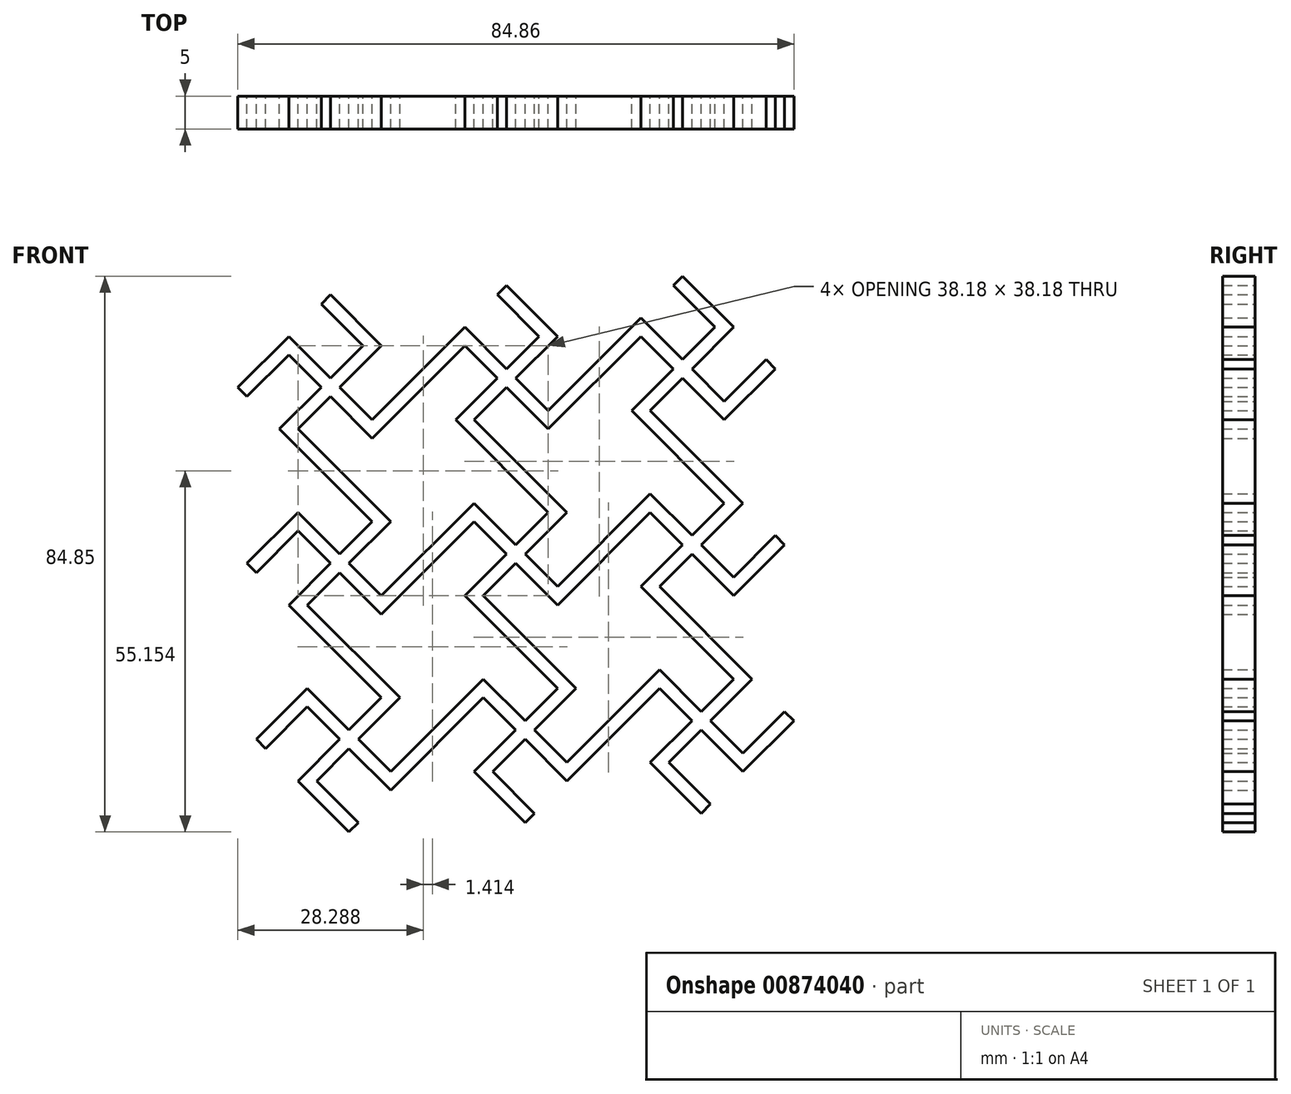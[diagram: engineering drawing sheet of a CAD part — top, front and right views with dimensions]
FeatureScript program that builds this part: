
annotation { "Feature Type Name" : "Feature", "Feature Type Description" : "" }
export const myFeature = defineFeature(function(context is Context, id is Id, definition is map)
    precondition{}
    {
        {
            var Q0;
            Q0=qCreatedBy(makeId("Front.planeOp"),FACE);
            var sketch = newSketch(context, id + "F0", { "sketchPlane" : qUnion([Q0])});
            skLineSegment(sketch, "E0", {"start": v(-7.07, 7.07) * mm, "end": v(-14.14, 0) * mm});
            skLineSegment(sketch, "E1", {"start": v(-7.07, -7.07) * mm, "end": v(0, -14.14) * mm});
            skLineSegment(sketch, "E2", {"start": v(7.07, -7.07) * mm, "end": v(14.14, 0) * mm});
            skLineSegment(sketch, "E3", {"start": v(7.07, 7.07) * mm, "end": v(0, 14.14) * mm});
            skLineSegment(sketch, "E4.bottom", {"start": v(6.36, 7.78) * mm, "end": v(7.78, 6.36) * mm});
            skLineSegment(sketch, "E4.top", {"start": v(-7.78, -6.36) * mm, "end": v(-6.36, -7.78) * mm});
            skLineSegment(sketch, "E4.left", {"start": v(4.95, 6.36) * mm, "end": v(0, 1.41) * mm});
            skLineSegment(sketch, "E4.right", {"start": v(7.78, 6.36) * mm, "end": v(1.41, 0) * mm});
            skPoint(sketch, "E4.middle", {"position": v(0, 0) * mm});
            skLineSegment(sketch, "E5.bottom", {"start": v(-6.36, 7.78) * mm, "end": v(0, 1.41) * mm});
            skLineSegment(sketch, "E5.top", {"start": v(-6.36, 4.95) * mm, "end": v(-1.41, 0) * mm});
            skLineSegment(sketch, "E5.left", {"start": v(-6.36, 7.78) * mm, "end": v(-7.78, 6.36) * mm});
            skLineSegment(sketch, "E5.right", {"start": v(7.78, -6.36) * mm, "end": v(6.36, -7.78) * mm});
            skPoint(sketch, "E6", {"position": v(-3.89, -10.25) * mm});
            skLineSegment(sketch, "E7.bottom", {"start": v(-6.36, 7.78) * mm, "end": v(-4.95, 6.36) * mm});
            skLineSegment(sketch, "E7.left", {"start": v(-6.36, 7.78) * mm, "end": v(-14.14, 0) * mm});
            skLineSegment(sketch, "E7.right", {"start": v(-6.36, 4.95) * mm, "end": v(-12.73, -1.41) * mm});
            skLineSegment(sketch, "E8.bottom", {"start": v(-7.78, -6.36) * mm, "end": v(0, -14.14) * mm});
            skLineSegment(sketch, "E8.top", {"start": v(-4.95, -6.36) * mm, "end": v(1.41, -12.73) * mm});
            skLineSegment(sketch, "E8.left", {"start": v(-7.78, -6.36) * mm, "end": v(-6.36, -4.95) * mm});
            skLineSegment(sketch, "E9.bottom", {"start": v(6.36, -7.78) * mm, "end": v(4.95, -6.36) * mm});
            skLineSegment(sketch, "E9.top", {"start": v(14.14, 0) * mm, "end": v(12.73, 1.41) * mm});
            skLineSegment(sketch, "E9.left", {"start": v(6.36, -7.78) * mm, "end": v(14.14, 0) * mm});
            skLineSegment(sketch, "E9.right", {"start": v(6.36, -4.95) * mm, "end": v(12.73, 1.41) * mm});
            skLineSegment(sketch, "E10.bottom", {"start": v(7.78, 6.36) * mm, "end": v(0, 14.14) * mm});
            skLineSegment(sketch, "E10.left", {"start": v(7.78, 6.36) * mm, "end": v(6.36, 4.95) * mm});
            skLineSegment(sketch, "E11.trimOffspring", {"start": v(4.95, 6.36) * mm, "end": v(-1.41, 12.73) * mm});
            skLineSegment(sketch, "E12.trimOffspring", {"start": v(1.41, 0) * mm, "end": v(6.36, -4.95) * mm});
            skLineSegment(sketch, "E13.trimOffspring", {"start": v(0, -1.41) * mm, "end": v(6.36, -7.78) * mm});
            skLineSegment(sketch, "E14.trimOffspring", {"start": v(0, -1.41) * mm, "end": v(-4.95, -6.36) * mm});
            skLineSegment(sketch, "E15.trimOffspring", {"start": v(-1.41, 0) * mm, "end": v(-7.78, -6.36) * mm});
            skLineSegment(sketch, "E16.0", {"start": v(12.73, 1.41) * mm, "end": v(14.14, 0) * mm, "construction": true});
            skLineSegment(sketch, "E17", {"start": v(-8.49, 33.94) * mm, "end": v(-15.56, 26.87) * mm});
            skLineSegment(sketch, "E18", {"start": v(-8.49, 19.8) * mm, "end": v(-1.41, 12.73) * mm});
            skLineSegment(sketch, "E19", {"start": v(5.66, 19.8) * mm, "end": v(12.73, 26.87) * mm});
            skLineSegment(sketch, "E20", {"start": v(5.66, 33.94) * mm, "end": v(-1.41, 41.01) * mm});
            skLineSegment(sketch, "E21.bottom", {"start": v(4.95, 34.65) * mm, "end": v(6.36, 33.23) * mm});
            skLineSegment(sketch, "E21.top", {"start": v(-9.2, 20.5) * mm, "end": v(-7.78, 19.1) * mm});
            skLineSegment(sketch, "E21.left", {"start": v(3.54, 33.23) * mm, "end": v(-1.41, 28.28) * mm});
            skLineSegment(sketch, "E21.right", {"start": v(6.36, 33.23) * mm, "end": v(0, 26.87) * mm});
            skPoint(sketch, "E21.middle", {"position": v(-1.41, 26.87) * mm});
            skLineSegment(sketch, "E22.bottom", {"start": v(-7.78, 34.65) * mm, "end": v(-1.41, 28.28) * mm});
            skLineSegment(sketch, "E22.top", {"start": v(-7.78, 31.82) * mm, "end": v(-2.83, 26.87) * mm});
            skLineSegment(sketch, "E22.left", {"start": v(-7.78, 34.65) * mm, "end": v(-9.2, 33.23) * mm});
            skLineSegment(sketch, "E22.right", {"start": v(6.36, 20.5) * mm, "end": v(4.95, 19.1) * mm});
            skPoint(sketch, "E23", {"position": v(-5.3, 16.62) * mm});
            skLineSegment(sketch, "E24.bottom", {"start": v(-7.78, 34.65) * mm, "end": v(-6.36, 33.23) * mm});
            skLineSegment(sketch, "E24.left", {"start": v(-7.78, 34.65) * mm, "end": v(-15.56, 26.87) * mm});
            skLineSegment(sketch, "E24.right", {"start": v(-7.78, 31.82) * mm, "end": v(-14.14, 25.46) * mm});
            skLineSegment(sketch, "E25.bottom", {"start": v(-9.2, 20.5) * mm, "end": v(-1.41, 12.73) * mm});
            skLineSegment(sketch, "E25.top", {"start": v(-6.36, 20.5) * mm, "end": v(0, 14.14) * mm});
            skLineSegment(sketch, "E25.left", {"start": v(-9.2, 20.5) * mm, "end": v(-7.78, 21.92) * mm});
            skLineSegment(sketch, "E26.bottom", {"start": v(4.95, 19.1) * mm, "end": v(3.54, 20.5) * mm});
            skLineSegment(sketch, "E26.top", {"start": v(12.73, 26.87) * mm, "end": v(11.31, 28.28) * mm});
            skLineSegment(sketch, "E26.left", {"start": v(4.95, 19.1) * mm, "end": v(12.73, 26.87) * mm});
            skLineSegment(sketch, "E26.right", {"start": v(4.95, 21.92) * mm, "end": v(11.31, 28.28) * mm});
            skLineSegment(sketch, "E27.bottom", {"start": v(6.36, 33.23) * mm, "end": v(-1.41, 41.01) * mm});
            skLineSegment(sketch, "E27.left", {"start": v(6.36, 33.23) * mm, "end": v(4.95, 31.82) * mm});
            skLineSegment(sketch, "E27.right", {"start": v(-1.41, 41.01) * mm, "end": v(-2.83, 39.6) * mm});
            skLineSegment(sketch, "E28.trimOffspring", {"start": v(3.54, 33.23) * mm, "end": v(-2.83, 39.6) * mm});
            skLineSegment(sketch, "E29.trimOffspring", {"start": v(0, 26.87) * mm, "end": v(4.95, 21.92) * mm});
            skLineSegment(sketch, "E30.trimOffspring", {"start": v(-1.41, 25.46) * mm, "end": v(4.95, 19.1) * mm});
            skLineSegment(sketch, "E31.trimOffspring", {"start": v(-1.41, 25.46) * mm, "end": v(-6.36, 20.5) * mm});
            skLineSegment(sketch, "E32.trimOffspring", {"start": v(-2.83, 26.87) * mm, "end": v(-9.2, 20.5) * mm});
            skLineSegment(sketch, "E33.0", {"start": v(11.31, 28.28) * mm, "end": v(12.73, 26.87) * mm, "construction": true});
            skLineSegment(sketch, "E34", {"start": v(-33.94, -8.49) * mm, "end": v(-26.87, -15.56) * mm});
            skLineSegment(sketch, "E35", {"start": v(-19.8, -8.49) * mm, "end": v(-12.73, -1.41) * mm});
            skLineSegment(sketch, "E36", {"start": v(-19.8, 5.66) * mm, "end": v(-26.87, 12.73) * mm});
            skLineSegment(sketch, "E37.bottom", {"start": v(-20.5, 6.36) * mm, "end": v(-19.1, 4.95) * mm});
            skLineSegment(sketch, "E37.top", {"start": v(-34.65, -7.78) * mm, "end": v(-33.23, -9.2) * mm});
            skLineSegment(sketch, "E37.left", {"start": v(-21.92, 4.95) * mm, "end": v(-26.87, 0) * mm});
            skLineSegment(sketch, "E37.right", {"start": v(-19.1, 4.95) * mm, "end": v(-25.46, -1.41) * mm});
            skPoint(sketch, "E37.middle", {"position": v(-26.87, -1.41) * mm});
            skLineSegment(sketch, "E38.bottom", {"start": v(-33.23, 6.36) * mm, "end": v(-26.87, 0) * mm});
            skLineSegment(sketch, "E38.top", {"start": v(-33.23, 3.54) * mm, "end": v(-28.28, -1.41) * mm});
            skLineSegment(sketch, "E38.left", {"start": v(-33.23, 6.36) * mm, "end": v(-34.65, 4.95) * mm});
            skLineSegment(sketch, "E38.right", {"start": v(-19.1, -7.78) * mm, "end": v(-20.5, -9.2) * mm});
            skPoint(sketch, "E39", {"position": v(-30.76, -11.67) * mm});
            skLineSegment(sketch, "E40.bottom", {"start": v(-33.23, 6.36) * mm, "end": v(-31.82, 4.95) * mm});
            skLineSegment(sketch, "E40.left", {"start": v(-33.23, 6.36) * mm, "end": v(-41.01, -1.41) * mm});
            skLineSegment(sketch, "E40.right", {"start": v(-33.23, 3.54) * mm, "end": v(-39.6, -2.83) * mm});
            skLineSegment(sketch, "E41.bottom", {"start": v(-34.65, -7.78) * mm, "end": v(-26.87, -15.56) * mm});
            skLineSegment(sketch, "E41.top", {"start": v(-31.82, -7.78) * mm, "end": v(-25.46, -14.14) * mm});
            skLineSegment(sketch, "E41.left", {"start": v(-34.65, -7.78) * mm, "end": v(-33.23, -6.36) * mm});
            skLineSegment(sketch, "E42.left", {"start": v(-20.5, -9.2) * mm, "end": v(-12.73, -1.41) * mm});
            skLineSegment(sketch, "E42.right", {"start": v(-20.5, -6.36) * mm, "end": v(-14.14, 0) * mm});
            skLineSegment(sketch, "E43.bottom", {"start": v(-19.1, 4.95) * mm, "end": v(-26.87, 12.73) * mm});
            skLineSegment(sketch, "E43.left", {"start": v(-19.1, 4.95) * mm, "end": v(-20.5, 3.54) * mm});
            skLineSegment(sketch, "E44.trimOffspring", {"start": v(-21.92, 4.95) * mm, "end": v(-28.28, 11.31) * mm});
            skLineSegment(sketch, "E45.trimOffspring", {"start": v(-25.46, -1.41) * mm, "end": v(-20.5, -6.36) * mm});
            skLineSegment(sketch, "E46.trimOffspring", {"start": v(-26.87, -2.83) * mm, "end": v(-20.5, -9.2) * mm});
            skLineSegment(sketch, "E47.trimOffspring", {"start": v(-26.87, -2.83) * mm, "end": v(-31.82, -7.78) * mm});
            skLineSegment(sketch, "E48.trimOffspring", {"start": v(-28.28, -1.41) * mm, "end": v(-34.65, -7.78) * mm});
            skLineSegment(sketch, "E49", {"start": v(-35.36, 32.53) * mm, "end": v(-42.43, 25.46) * mm});
            skLineSegment(sketch, "E50", {"start": v(-35.36, 18.38) * mm, "end": v(-28.28, 11.31) * mm});
            skLineSegment(sketch, "E51", {"start": v(-21.21, 18.38) * mm, "end": v(-14.14, 25.46) * mm});
            skLineSegment(sketch, "E52", {"start": v(-21.21, 32.53) * mm, "end": v(-28.28, 39.6) * mm});
            skLineSegment(sketch, "E53.bottom", {"start": v(-21.92, 33.23) * mm, "end": v(-20.5, 31.82) * mm});
            skLineSegment(sketch, "E53.top", {"start": v(-36.06, 19.1) * mm, "end": v(-34.65, 17.68) * mm});
            skLineSegment(sketch, "E53.left", {"start": v(-23.33, 31.82) * mm, "end": v(-28.28, 26.87) * mm});
            skLineSegment(sketch, "E53.right", {"start": v(-20.5, 31.82) * mm, "end": v(-26.87, 25.46) * mm});
            skPoint(sketch, "E53.middle", {"position": v(-28.28, 25.46) * mm});
            skLineSegment(sketch, "E54.bottom", {"start": v(-34.65, 33.23) * mm, "end": v(-28.28, 26.87) * mm});
            skLineSegment(sketch, "E54.top", {"start": v(-34.65, 30.4) * mm, "end": v(-29.7, 25.46) * mm});
            skLineSegment(sketch, "E54.left", {"start": v(-34.65, 33.23) * mm, "end": v(-36.06, 31.82) * mm});
            skLineSegment(sketch, "E54.right", {"start": v(-20.5, 19.1) * mm, "end": v(-21.92, 17.68) * mm});
            skPoint(sketch, "E55", {"position": v(-32.17, 15.2) * mm});
            skLineSegment(sketch, "E56.bottom", {"start": v(-34.65, 33.23) * mm, "end": v(-33.23, 31.82) * mm});
            skLineSegment(sketch, "E56.left", {"start": v(-34.65, 33.23) * mm, "end": v(-42.43, 25.46) * mm});
            skLineSegment(sketch, "E56.right", {"start": v(-34.65, 30.4) * mm, "end": v(-41.01, 24.04) * mm});
            skLineSegment(sketch, "E57.bottom", {"start": v(-36.06, 19.1) * mm, "end": v(-28.28, 11.31) * mm});
            skLineSegment(sketch, "E57.top", {"start": v(-33.23, 19.1) * mm, "end": v(-26.87, 12.73) * mm});
            skLineSegment(sketch, "E57.left", {"start": v(-36.06, 19.1) * mm, "end": v(-34.65, 20.5) * mm});
            skLineSegment(sketch, "E58.bottom", {"start": v(-21.92, 17.68) * mm, "end": v(-23.33, 19.1) * mm});
            skLineSegment(sketch, "E58.left", {"start": v(-21.92, 17.68) * mm, "end": v(-14.14, 25.46) * mm});
            skLineSegment(sketch, "E58.right", {"start": v(-21.92, 20.5) * mm, "end": v(-15.56, 26.87) * mm});
            skLineSegment(sketch, "E59.bottom", {"start": v(-20.5, 31.82) * mm, "end": v(-28.28, 39.6) * mm});
            skLineSegment(sketch, "E59.left", {"start": v(-20.5, 31.82) * mm, "end": v(-21.92, 30.4) * mm});
            skLineSegment(sketch, "E59.right", {"start": v(-28.28, 39.6) * mm, "end": v(-29.7, 38.18) * mm});
            skLineSegment(sketch, "E60.trimOffspring", {"start": v(-23.33, 31.82) * mm, "end": v(-29.7, 38.18) * mm});
            skLineSegment(sketch, "E61.trimOffspring", {"start": v(-26.87, 25.46) * mm, "end": v(-21.92, 20.5) * mm});
            skLineSegment(sketch, "E62.trimOffspring", {"start": v(-28.28, 24.04) * mm, "end": v(-21.92, 17.68) * mm});
            skLineSegment(sketch, "E63.trimOffspring", {"start": v(-28.28, 24.04) * mm, "end": v(-33.23, 19.1) * mm});
            skLineSegment(sketch, "E64.trimOffspring", {"start": v(-29.7, 25.46) * mm, "end": v(-36.06, 19.1) * mm});
            skLineSegment(sketch, "E65", {"start": v(-62.23, 31.11) * mm, "end": v(-69.3, 24.04) * mm});
            skLineSegment(sketch, "E66", {"start": v(-62.23, 16.97) * mm, "end": v(-55.15, 9.9) * mm});
            skLineSegment(sketch, "E67", {"start": v(-48.08, 16.97) * mm, "end": v(-41.01, 24.04) * mm});
            skLineSegment(sketch, "E68", {"start": v(-48.08, 31.11) * mm, "end": v(-55.15, 38.18) * mm});
            skLineSegment(sketch, "E69.bottom", {"start": v(-48.8, 31.82) * mm, "end": v(-47.38, 30.4) * mm});
            skLineSegment(sketch, "E69.top", {"start": v(-62.93, 17.68) * mm, "end": v(-61.52, 16.26) * mm});
            skLineSegment(sketch, "E69.left", {"start": v(-50.2, 30.4) * mm, "end": v(-55.15, 25.46) * mm});
            skLineSegment(sketch, "E69.right", {"start": v(-47.38, 30.4) * mm, "end": v(-53.74, 24.04) * mm});
            skPoint(sketch, "E69.middle", {"position": v(-55.15, 24.04) * mm});
            skLineSegment(sketch, "E70.bottom", {"start": v(-61.52, 31.82) * mm, "end": v(-55.15, 25.46) * mm});
            skLineSegment(sketch, "E70.top", {"start": v(-61.52, 29) * mm, "end": v(-56.57, 24.04) * mm});
            skLineSegment(sketch, "E70.left", {"start": v(-61.52, 31.82) * mm, "end": v(-62.93, 30.4) * mm});
            skLineSegment(sketch, "E70.right", {"start": v(-47.38, 17.68) * mm, "end": v(-48.8, 16.26) * mm});
            skPoint(sketch, "E71", {"position": v(-59.04, 13.79) * mm});
            skLineSegment(sketch, "E72.bottom", {"start": v(-61.52, 31.82) * mm, "end": v(-60.1, 30.4) * mm});
            skLineSegment(sketch, "E72.top", {"start": v(-69.3, 24.04) * mm, "end": v(-67.88, 22.63) * mm});
            skLineSegment(sketch, "E72.left", {"start": v(-61.52, 31.82) * mm, "end": v(-69.3, 24.04) * mm});
            skLineSegment(sketch, "E72.right", {"start": v(-61.52, 29) * mm, "end": v(-67.88, 22.63) * mm});
            skLineSegment(sketch, "E73.bottom", {"start": v(-62.93, 17.68) * mm, "end": v(-55.15, 9.9) * mm});
            skLineSegment(sketch, "E73.top", {"start": v(-60.1, 17.68) * mm, "end": v(-53.74, 11.31) * mm});
            skLineSegment(sketch, "E73.left", {"start": v(-62.93, 17.68) * mm, "end": v(-61.52, 19.1) * mm});
            skLineSegment(sketch, "E74.bottom", {"start": v(-48.8, 16.26) * mm, "end": v(-50.2, 17.68) * mm});
            skLineSegment(sketch, "E74.left", {"start": v(-48.8, 16.26) * mm, "end": v(-41.01, 24.04) * mm});
            skLineSegment(sketch, "E74.right", {"start": v(-48.8, 19.1) * mm, "end": v(-42.43, 25.46) * mm});
            skLineSegment(sketch, "E75.bottom", {"start": v(-47.38, 30.4) * mm, "end": v(-55.15, 38.18) * mm});
            skLineSegment(sketch, "E75.left", {"start": v(-47.38, 30.4) * mm, "end": v(-48.8, 29) * mm});
            skLineSegment(sketch, "E75.right", {"start": v(-55.15, 38.18) * mm, "end": v(-56.57, 36.77) * mm});
            skLineSegment(sketch, "E76.trimOffspring", {"start": v(-50.2, 30.4) * mm, "end": v(-56.57, 36.77) * mm});
            skLineSegment(sketch, "E77.trimOffspring", {"start": v(-53.74, 24.04) * mm, "end": v(-48.8, 19.1) * mm});
            skLineSegment(sketch, "E78.trimOffspring", {"start": v(-55.15, 22.63) * mm, "end": v(-48.8, 16.26) * mm});
            skLineSegment(sketch, "E79.trimOffspring", {"start": v(-55.15, 22.63) * mm, "end": v(-60.1, 17.68) * mm});
            skLineSegment(sketch, "E80.trimOffspring", {"start": v(-56.57, 24.04) * mm, "end": v(-62.93, 17.68) * mm});
            skLineSegment(sketch, "E81.0", {"start": v(-69.3, 24.04) * mm, "end": v(-67.88, 22.63) * mm, "construction": true});
            skLineSegment(sketch, "E82", {"start": v(-60.81, 4.24) * mm, "end": v(-67.88, -2.83) * mm});
            skLineSegment(sketch, "E83", {"start": v(-60.81, -9.9) * mm, "end": v(-53.74, -16.97) * mm});
            skLineSegment(sketch, "E84", {"start": v(-46.67, -9.9) * mm, "end": v(-39.6, -2.83) * mm});
            skLineSegment(sketch, "E85", {"start": v(-46.67, 4.24) * mm, "end": v(-53.74, 11.31) * mm});
            skLineSegment(sketch, "E86.bottom", {"start": v(-47.38, 4.95) * mm, "end": v(-45.96, 3.54) * mm});
            skLineSegment(sketch, "E86.top", {"start": v(-61.52, -9.2) * mm, "end": v(-60.1, -10.6) * mm});
            skLineSegment(sketch, "E86.left", {"start": v(-48.8, 3.54) * mm, "end": v(-53.74, -1.41) * mm});
            skLineSegment(sketch, "E86.right", {"start": v(-45.96, 3.54) * mm, "end": v(-52.33, -2.83) * mm});
            skPoint(sketch, "E86.middle", {"position": v(-53.74, -2.83) * mm});
            skLineSegment(sketch, "E87.bottom", {"start": v(-60.1, 4.95) * mm, "end": v(-53.74, -1.41) * mm});
            skLineSegment(sketch, "E87.top", {"start": v(-60.1, 2.12) * mm, "end": v(-55.15, -2.83) * mm});
            skLineSegment(sketch, "E87.left", {"start": v(-60.1, 4.95) * mm, "end": v(-61.52, 3.54) * mm});
            skLineSegment(sketch, "E87.right", {"start": v(-45.96, -9.2) * mm, "end": v(-47.38, -10.6) * mm});
            skPoint(sketch, "E88", {"position": v(-57.63, -13.08) * mm});
            skLineSegment(sketch, "E89.bottom", {"start": v(-60.1, 4.95) * mm, "end": v(-58.69, 3.54) * mm});
            skLineSegment(sketch, "E89.top", {"start": v(-67.88, -2.83) * mm, "end": v(-66.47, -4.24) * mm});
            skLineSegment(sketch, "E89.left", {"start": v(-60.1, 4.95) * mm, "end": v(-67.88, -2.83) * mm});
            skLineSegment(sketch, "E89.right", {"start": v(-60.1, 2.12) * mm, "end": v(-66.47, -4.24) * mm});
            skLineSegment(sketch, "E90.bottom", {"start": v(-61.52, -9.2) * mm, "end": v(-53.74, -16.97) * mm});
            skLineSegment(sketch, "E90.top", {"start": v(-58.69, -9.2) * mm, "end": v(-52.33, -15.56) * mm});
            skLineSegment(sketch, "E90.left", {"start": v(-61.52, -9.2) * mm, "end": v(-60.1, -7.78) * mm});
            skLineSegment(sketch, "E91.bottom", {"start": v(-47.38, -10.6) * mm, "end": v(-48.8, -9.2) * mm});
            skLineSegment(sketch, "E91.left", {"start": v(-47.38, -10.6) * mm, "end": v(-39.6, -2.83) * mm});
            skLineSegment(sketch, "E91.right", {"start": v(-47.38, -7.78) * mm, "end": v(-41.01, -1.41) * mm});
            skLineSegment(sketch, "E92.bottom", {"start": v(-45.96, 3.54) * mm, "end": v(-53.74, 11.31) * mm});
            skLineSegment(sketch, "E92.left", {"start": v(-45.96, 3.54) * mm, "end": v(-47.38, 2.12) * mm});
            skLineSegment(sketch, "E93.trimOffspring", {"start": v(-48.8, 3.54) * mm, "end": v(-55.15, 9.9) * mm});
            skLineSegment(sketch, "E94.trimOffspring", {"start": v(-52.33, -2.83) * mm, "end": v(-47.38, -7.78) * mm});
            skLineSegment(sketch, "E95.trimOffspring", {"start": v(-53.74, -4.24) * mm, "end": v(-47.38, -10.6) * mm});
            skLineSegment(sketch, "E96.trimOffspring", {"start": v(-53.74, -4.24) * mm, "end": v(-58.69, -9.2) * mm});
            skLineSegment(sketch, "E97.trimOffspring", {"start": v(-55.15, -2.83) * mm, "end": v(-61.52, -9.2) * mm});
            skLineSegment(sketch, "E98", {"start": v(-59.4, -22.63) * mm, "end": v(-66.47, -29.7) * mm});
            skLineSegment(sketch, "E99", {"start": v(-59.4, -36.77) * mm, "end": v(-52.33, -43.84) * mm});
            skLineSegment(sketch, "E100", {"start": v(-45.25, -36.77) * mm, "end": v(-38.18, -29.7) * mm});
            skLineSegment(sketch, "E101", {"start": v(-45.25, -22.63) * mm, "end": v(-52.33, -15.56) * mm});
            skLineSegment(sketch, "E102.bottom", {"start": v(-45.96, -21.92) * mm, "end": v(-44.55, -23.33) * mm});
            skLineSegment(sketch, "E102.top", {"start": v(-60.1, -36.06) * mm, "end": v(-58.69, -37.48) * mm});
            skLineSegment(sketch, "E102.left", {"start": v(-47.38, -23.33) * mm, "end": v(-52.33, -28.28) * mm});
            skLineSegment(sketch, "E102.right", {"start": v(-44.55, -23.33) * mm, "end": v(-50.91, -29.7) * mm});
            skPoint(sketch, "E102.middle", {"position": v(-52.33, -29.7) * mm});
            skLineSegment(sketch, "E103.bottom", {"start": v(-58.69, -21.92) * mm, "end": v(-52.33, -28.28) * mm});
            skLineSegment(sketch, "E103.top", {"start": v(-58.69, -24.75) * mm, "end": v(-53.74, -29.7) * mm});
            skLineSegment(sketch, "E103.left", {"start": v(-58.69, -21.92) * mm, "end": v(-60.1, -23.33) * mm});
            skLineSegment(sketch, "E103.right", {"start": v(-44.55, -36.06) * mm, "end": v(-45.96, -37.48) * mm});
            skPoint(sketch, "E104", {"position": v(-56.21, -39.95) * mm});
            skLineSegment(sketch, "E105.bottom", {"start": v(-58.69, -21.92) * mm, "end": v(-57.28, -23.33) * mm});
            skLineSegment(sketch, "E105.top", {"start": v(-66.47, -29.7) * mm, "end": v(-65.05, -31.11) * mm});
            skLineSegment(sketch, "E105.left", {"start": v(-58.69, -21.92) * mm, "end": v(-66.47, -29.7) * mm});
            skLineSegment(sketch, "E105.right", {"start": v(-58.69, -24.75) * mm, "end": v(-65.05, -31.11) * mm});
            skLineSegment(sketch, "E106.bottom", {"start": v(-60.1, -36.06) * mm, "end": v(-52.33, -43.84) * mm});
            skLineSegment(sketch, "E106.top", {"start": v(-57.28, -36.06) * mm, "end": v(-50.91, -42.43) * mm});
            skLineSegment(sketch, "E106.left", {"start": v(-60.1, -36.06) * mm, "end": v(-58.69, -34.65) * mm});
            skLineSegment(sketch, "E106.right", {"start": v(-52.33, -43.84) * mm, "end": v(-50.91, -42.43) * mm});
            skLineSegment(sketch, "E107.bottom", {"start": v(-45.96, -37.48) * mm, "end": v(-47.38, -36.06) * mm});
            skLineSegment(sketch, "E107.left", {"start": v(-45.96, -37.48) * mm, "end": v(-38.18, -29.7) * mm});
            skLineSegment(sketch, "E107.right", {"start": v(-45.96, -34.65) * mm, "end": v(-39.6, -28.28) * mm});
            skLineSegment(sketch, "E108.bottom", {"start": v(-44.55, -23.33) * mm, "end": v(-52.33, -15.56) * mm});
            skLineSegment(sketch, "E108.left", {"start": v(-44.55, -23.33) * mm, "end": v(-45.96, -24.75) * mm});
            skLineSegment(sketch, "E109.trimOffspring", {"start": v(-47.38, -23.33) * mm, "end": v(-53.74, -16.97) * mm});
            skLineSegment(sketch, "E110.trimOffspring", {"start": v(-50.91, -29.7) * mm, "end": v(-45.96, -34.65) * mm});
            skLineSegment(sketch, "E111.trimOffspring", {"start": v(-52.33, -31.11) * mm, "end": v(-45.96, -37.48) * mm});
            skLineSegment(sketch, "E112.trimOffspring", {"start": v(-52.33, -31.11) * mm, "end": v(-57.28, -36.06) * mm});
            skLineSegment(sketch, "E113.trimOffspring", {"start": v(-53.74, -29.7) * mm, "end": v(-60.1, -36.06) * mm});
            skLineSegment(sketch, "E114.0", {"start": v(-66.47, -29.7) * mm, "end": v(-65.05, -31.11) * mm, "construction": true});
            skLineSegment(sketch, "E115.0", {"start": v(-52.33, -43.84) * mm, "end": v(-50.91, -42.43) * mm, "construction": true});
            skLineSegment(sketch, "E116", {"start": v(-32.53, -21.21) * mm, "end": v(-39.6, -28.28) * mm});
            skLineSegment(sketch, "E117", {"start": v(-32.53, -35.36) * mm, "end": v(-25.46, -42.43) * mm});
            skLineSegment(sketch, "E118", {"start": v(-18.38, -35.36) * mm, "end": v(-11.31, -28.28) * mm});
            skLineSegment(sketch, "E119", {"start": v(-18.38, -21.21) * mm, "end": v(-25.46, -14.14) * mm});
            skLineSegment(sketch, "E120.bottom", {"start": v(-19.1, -20.5) * mm, "end": v(-17.68, -21.92) * mm});
            skLineSegment(sketch, "E120.top", {"start": v(-33.23, -34.65) * mm, "end": v(-31.82, -36.06) * mm});
            skLineSegment(sketch, "E120.left", {"start": v(-20.5, -21.92) * mm, "end": v(-25.46, -26.87) * mm});
            skLineSegment(sketch, "E120.right", {"start": v(-17.68, -21.92) * mm, "end": v(-24.04, -28.28) * mm});
            skPoint(sketch, "E120.middle", {"position": v(-25.46, -28.28) * mm});
            skLineSegment(sketch, "E121.bottom", {"start": v(-31.82, -20.5) * mm, "end": v(-25.46, -26.87) * mm});
            skLineSegment(sketch, "E121.top", {"start": v(-31.82, -23.33) * mm, "end": v(-26.87, -28.28) * mm});
            skLineSegment(sketch, "E121.left", {"start": v(-31.82, -20.5) * mm, "end": v(-33.23, -21.92) * mm});
            skLineSegment(sketch, "E121.right", {"start": v(-17.68, -34.65) * mm, "end": v(-19.1, -36.06) * mm});
            skPoint(sketch, "E122", {"position": v(-29.34, -38.54) * mm});
            skLineSegment(sketch, "E123.bottom", {"start": v(-31.82, -20.5) * mm, "end": v(-30.4, -21.92) * mm});
            skLineSegment(sketch, "E123.left", {"start": v(-31.82, -20.5) * mm, "end": v(-39.6, -28.28) * mm});
            skLineSegment(sketch, "E123.right", {"start": v(-31.82, -23.33) * mm, "end": v(-38.18, -29.7) * mm});
            skLineSegment(sketch, "E124.bottom", {"start": v(-33.23, -34.65) * mm, "end": v(-25.46, -42.43) * mm});
            skLineSegment(sketch, "E124.top", {"start": v(-30.4, -34.65) * mm, "end": v(-24.04, -41.01) * mm});
            skLineSegment(sketch, "E124.left", {"start": v(-33.23, -34.65) * mm, "end": v(-31.82, -33.23) * mm});
            skLineSegment(sketch, "E124.right", {"start": v(-25.46, -42.43) * mm, "end": v(-24.04, -41.01) * mm});
            skLineSegment(sketch, "E125.bottom", {"start": v(-19.1, -36.06) * mm, "end": v(-20.5, -34.65) * mm});
            skLineSegment(sketch, "E125.left", {"start": v(-19.1, -36.06) * mm, "end": v(-11.31, -28.28) * mm});
            skLineSegment(sketch, "E125.right", {"start": v(-19.1, -33.23) * mm, "end": v(-12.73, -26.87) * mm});
            skLineSegment(sketch, "E126.bottom", {"start": v(-17.68, -21.92) * mm, "end": v(-25.46, -14.14) * mm});
            skLineSegment(sketch, "E126.left", {"start": v(-17.68, -21.92) * mm, "end": v(-19.1, -23.33) * mm});
            skLineSegment(sketch, "E127.trimOffspring", {"start": v(-20.5, -21.92) * mm, "end": v(-26.87, -15.56) * mm});
            skLineSegment(sketch, "E128.trimOffspring", {"start": v(-25.46, -29.7) * mm, "end": v(-19.1, -36.06) * mm});
            skLineSegment(sketch, "E129.trimOffspring", {"start": v(-25.46, -29.7) * mm, "end": v(-30.4, -34.65) * mm});
            skLineSegment(sketch, "E130.trimOffspring", {"start": v(-26.87, -28.28) * mm, "end": v(-33.23, -34.65) * mm});
            skLineSegment(sketch, "E131.0", {"start": v(-25.46, -42.43) * mm, "end": v(-24.04, -41.01) * mm, "construction": true});
            skLineSegment(sketch, "E132", {"start": v(-5.66, -19.8) * mm, "end": v(-12.73, -26.87) * mm});
            skLineSegment(sketch, "E133", {"start": v(-5.66, -33.94) * mm, "end": v(1.41, -41.01) * mm});
            skLineSegment(sketch, "E134", {"start": v(8.49, -33.94) * mm, "end": v(15.56, -26.87) * mm});
            skLineSegment(sketch, "E135", {"start": v(8.49, -19.8) * mm, "end": v(1.41, -12.73) * mm});
            skLineSegment(sketch, "E136.bottom", {"start": v(7.78, -19.1) * mm, "end": v(9.2, -20.5) * mm});
            skLineSegment(sketch, "E136.top", {"start": v(-6.36, -33.23) * mm, "end": v(-4.95, -34.65) * mm});
            skLineSegment(sketch, "E136.left", {"start": v(6.36, -20.5) * mm, "end": v(1.41, -25.46) * mm});
            skLineSegment(sketch, "E136.right", {"start": v(9.2, -20.5) * mm, "end": v(2.83, -26.87) * mm});
            skPoint(sketch, "E136.middle", {"position": v(1.41, -26.87) * mm});
            skLineSegment(sketch, "E137.bottom", {"start": v(-4.95, -19.1) * mm, "end": v(1.41, -25.46) * mm});
            skLineSegment(sketch, "E137.top", {"start": v(-4.95, -21.92) * mm, "end": v(0, -26.87) * mm});
            skLineSegment(sketch, "E137.left", {"start": v(-4.95, -19.1) * mm, "end": v(-6.36, -20.5) * mm});
            skLineSegment(sketch, "E137.right", {"start": v(9.2, -33.23) * mm, "end": v(7.78, -34.65) * mm});
            skPoint(sketch, "E138", {"position": v(-2.47, -37.12) * mm});
            skLineSegment(sketch, "E139.bottom", {"start": v(-4.95, -19.1) * mm, "end": v(-3.54, -20.5) * mm});
            skLineSegment(sketch, "E139.left", {"start": v(-4.95, -19.1) * mm, "end": v(-12.73, -26.87) * mm});
            skLineSegment(sketch, "E139.right", {"start": v(-4.95, -21.92) * mm, "end": v(-11.31, -28.28) * mm});
            skLineSegment(sketch, "E140.bottom", {"start": v(-6.36, -33.23) * mm, "end": v(1.41, -41.01) * mm});
            skLineSegment(sketch, "E140.top", {"start": v(-3.54, -33.23) * mm, "end": v(2.83, -39.6) * mm});
            skLineSegment(sketch, "E140.left", {"start": v(-6.36, -33.23) * mm, "end": v(-4.95, -31.82) * mm});
            skLineSegment(sketch, "E140.right", {"start": v(1.41, -41.01) * mm, "end": v(2.83, -39.6) * mm});
            skLineSegment(sketch, "E141.bottom", {"start": v(7.78, -34.65) * mm, "end": v(6.36, -33.23) * mm});
            skLineSegment(sketch, "E141.top", {"start": v(15.56, -26.87) * mm, "end": v(14.14, -25.46) * mm});
            skLineSegment(sketch, "E141.left", {"start": v(7.78, -34.65) * mm, "end": v(15.56, -26.87) * mm});
            skLineSegment(sketch, "E141.right", {"start": v(7.78, -31.82) * mm, "end": v(14.14, -25.46) * mm});
            skLineSegment(sketch, "E142.bottom", {"start": v(9.2, -20.5) * mm, "end": v(1.41, -12.73) * mm});
            skLineSegment(sketch, "E142.left", {"start": v(9.2, -20.5) * mm, "end": v(7.78, -21.92) * mm});
            skLineSegment(sketch, "E143.trimOffspring", {"start": v(6.36, -20.5) * mm, "end": v(0, -14.14) * mm});
            skLineSegment(sketch, "E144.trimOffspring", {"start": v(2.83, -26.87) * mm, "end": v(7.78, -31.82) * mm});
            skLineSegment(sketch, "E145.trimOffspring", {"start": v(1.41, -28.28) * mm, "end": v(7.78, -34.65) * mm});
            skLineSegment(sketch, "E146.trimOffspring", {"start": v(1.41, -28.28) * mm, "end": v(-3.54, -33.23) * mm});
            skLineSegment(sketch, "E147.trimOffspring", {"start": v(0, -26.87) * mm, "end": v(-6.36, -33.23) * mm});
            skLineSegment(sketch, "E148.0", {"start": v(14.14, -25.46) * mm, "end": v(15.56, -26.87) * mm, "construction": true});
            skLineSegment(sketch, "E149.0", {"start": v(1.41, -41.01) * mm, "end": v(2.83, -39.6) * mm, "construction": true});
            skLineSegment(sketch, "E150", {"start": v(-24.04, -28.28) * mm, "end": v(-19.1, -33.23) * mm});
            skSolve(sketch);
        }
        {
            var Q0;
            Q0 = qSketchRegion(id + "F0", true);
            extrude(context, id + "F1", {"entities" : qUnion([Q0]), "depth" : 5 * mm, "offsetDistance" : 25 * mm});
        }
    });
